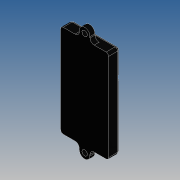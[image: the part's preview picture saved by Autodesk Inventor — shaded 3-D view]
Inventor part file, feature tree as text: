
AUTODESK INVENTOR PART (.ipt)
format: ipt  version: 2019 (Build 230136000, 136)  size: 582,144 bytes
history: native  units: mm
features: sketch x15, extrude x10, fillet x7, mirror x5, plane x4, sweep x2, chamfer x2, shell x1, hole x1, projected_geometry x1
ambient origin geometry x8: Origin, YZ Plane, XZ Plane, XY Plane, X Axis, Y Axis, Z Axis, Center Point
bodies: Solid1 (feature_tree)
feature tree (48):
  extrude  "Extrusion1"  Depth=29.0mm
  shell  "Shell1"  Thickness=112.0mm
  extrude  "Extrusion2"  Depth=2.0mm
  fillet  "Fillet1"  Radius=30.0mm
  fillet  "Fillet2"  Radius=130.0mm
  extrude  "Extrusion3"  Depth=1.0mm
  fillet  "Fillet3"  Radius=3.2mm
  extrude  "Extrusion4"  Depth=2.0mm
  fillet  "Fillet6"  Radius=2.0mm
  hole  "Hole1"  [1 undecoded]
  plane  "Work Plane1"
  fillet  "Fillet7"  Radius=3.0mm
  mirror  "Mirror3"
  mirror  "Mirror4"
  extrude  "Extrusion6"  Depth=6.5mm
  sweep  "Sweep1"
  sweep  "Sweep3"
  fillet  "Fillet8"  Radius=3.2mm
  mirror  "Mirror1"
  extrude  "Extrusion5"  Depth=12.0mm
  extrude  "Extrusion7"  Depth=6.0mm TaperAngle=0.0deg
  plane  "Work Plane2"
  extrude  "Extrusion8"  Depth=2.5mm
  extrude  "Extrusion9"  Depth=0.3mm
  extrude  "Extrusion10"  Depth=2.0mm
  chamfer  "Chamfer1"  Distance=2.0mm
  chamfer  "Chamfer2"  Distance=1.0mm
  fillet  "Fillet9"  Radius=1.0mm
  plane  "Work Plane3"
  mirror  "Mirror5"
  plane  "Work Plane4"
  mirror  "Mirror6"
  sketch  "Sketch1"  dims[d0=11.0mm d1=29.0mm d2=112.0mm d3=0.0mm]
  sketch  "Sketch2"  dims[d4=2.0mm d5=2.0mm d6=30.0mm d7=130.0mm d8=0.0mm]
  sketch  "Sketch3"  dims[d9=1.0mm d10=1.0mm d11=3.2mm]
  sketch  "Sketch4"  dims[d12=2.0mm d13=2.0mm d14=2.0mm]
  sketch  "Sketch5"  dims[d15=24.0mm d16=130.0mm d17=0.0mm d18=3.0mm]
  sketch  "Sketch6"  dims[d21=13.0mm d22=6.5mm]
  sketch  "Sketch7"  dims[d23=6.0mm d24=0.0mm d25=6.5mm]
  sketch  "Sketch8"  dims[d26=6.5mm d27=6.0mm d28=4.0mm d29=2.0mm d30=90.0deg d31=8.0mm d32=20.594885mm d33=5.0mm d34=3.2mm]
  sketch  "3D Sketch1"
  sketch  "Sketch10"  dims[d35=4.2mm d36=12.0mm]
  sketch  "Sketch11"  dims[d37=12.0mm d38=6.0mm d39=0.0mm]
  sketch  "3D Sketch3"
  sketch  "Sketch12"  dims[d40=2.0mm d42=2.0mm d43=0.0mm d44=2.5mm]
  sketch  "Sketch13"  dims[d45=0.8mm d46=0.3mm]
  sketch  "Sketch14"  dims[d47=0.0mm d48=0.0mm d53=2.0mm d55=2.0mm d56=0.0mm d57=1.0mm d58=1.0mm d59=0.3mm d60=0.8mm d61=0.0mm d62=0.0mm d63=0.4mm d64=2.0mm d65=3.5mm d66=3.5mm d69=2.0mm d70=0.0mm d71=1.5mm d72=1.5mm d73=1.8mm d74=0.0mm d75=0.4mm d76=0.4mm d77=2.0mm d78=0.0mm d79=2.0mm d80=2.0mm d81=15.0deg d82=2.0mm d83=2.0mm d84=15.0deg d85=0.4mm d86=19.9mm d87=15.5mm]
  projected_geometry  "Project Cut Edges1"
note: 1 required parameter value undecoded (feature->parameter linkage not recoverable at this tier; creation-order binding heuristic only, values carry confidence <= 0.55)
